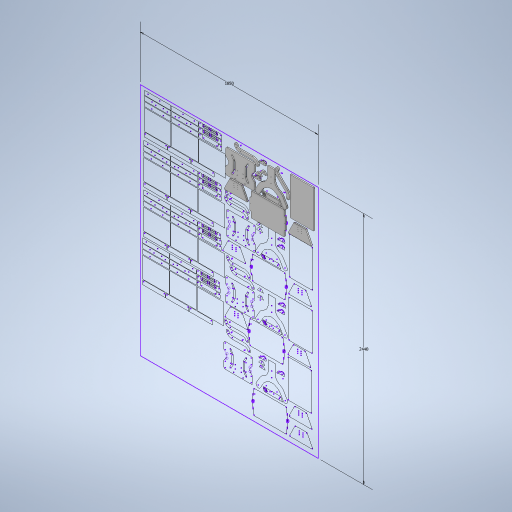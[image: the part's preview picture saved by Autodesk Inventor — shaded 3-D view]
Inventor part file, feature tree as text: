
AUTODESK INVENTOR PART (.ipt)
format: ipt  version: 2024 (Build 280153000, 153)  size: 1,304,064 bytes
history: native  units: mm
features: other x14, extrude x13
ambient origin geometry x8: Origin, YZ Plane, XZ Plane, XY Plane, X Axis, Y Axis, Z Axis, Center Point
bodies: Body1 (feature_tree), Body2 (feature_tree), Body3 (feature_tree), Body4 (feature_tree), Body5 (feature_tree), Body6 (feature_tree), Body7 (feature_tree), Body8 (feature_tree), Body9 (feature_tree), Body10 (feature_tree), Body11 (feature_tree), Body12 (feature_tree), Body13 (feature_tree)
feature tree (27):
  other  "PLACA_SOPORTE_1"
  other  "Visible"
  extrude  "Extrusión1"  Depth=1850.0mm
  extrude  "Extrusión2"  Depth=2440.0mm
  extrude  "Extrusión3"  Depth=12.0mm TaperAngle=0.0deg
  extrude  "Extrusión4"  Depth=12.0mm TaperAngle=0.0deg
  extrude  "Extrusión5"  Depth=12.0mm TaperAngle=0.0deg
  extrude  "Extrusión6"  Depth=12.0mm TaperAngle=0.0deg
  extrude  "Extrusión7"  Depth=12.0mm TaperAngle=0.0deg
  extrude  "Extrusión8"  Depth=12.0mm TaperAngle=0.0deg
  extrude  "Extrusión9"  Depth=12.0mm TaperAngle=0.0deg
  extrude  "Extrusión10"  Depth=12.0mm TaperAngle=0.0deg
  extrude  "Extrusión11"  Depth=12.0mm TaperAngle=0.0deg
  extrude  "Extrusión12"  Depth=12.0mm TaperAngle=0.0deg
  extrude  "Extrusión13"  Depth=12.0mm TaperAngle=0.0deg
  other  "BASE_SOPORTE_1"
  other  "GRADUADOR_INCLINACION_SOPORTE_1"
  other  "SUJECION_CENTRAL_SOPORTE_1"
  other  "SOPORTE_LATERAL_SOPORTE_1"
  other  "SOPORTE_LATERAL_2_SOPORTE_1"
  other  "GRADUADOR_INCLINACION_2_SOPORTE_1"
  other  "BRAZO_SOPORTE_1"
  other  "BRAZO_2_SOPORTE_1"
  other  "PLACA_INFERIOR_MESA_1"
  other  "PLACA_SUPERIOR_MESA_1"
  other  "SOPORTE_LATERAL_I_MESA_1"
  other  "SOPORTE_LATERAL_D_MESA_1"
